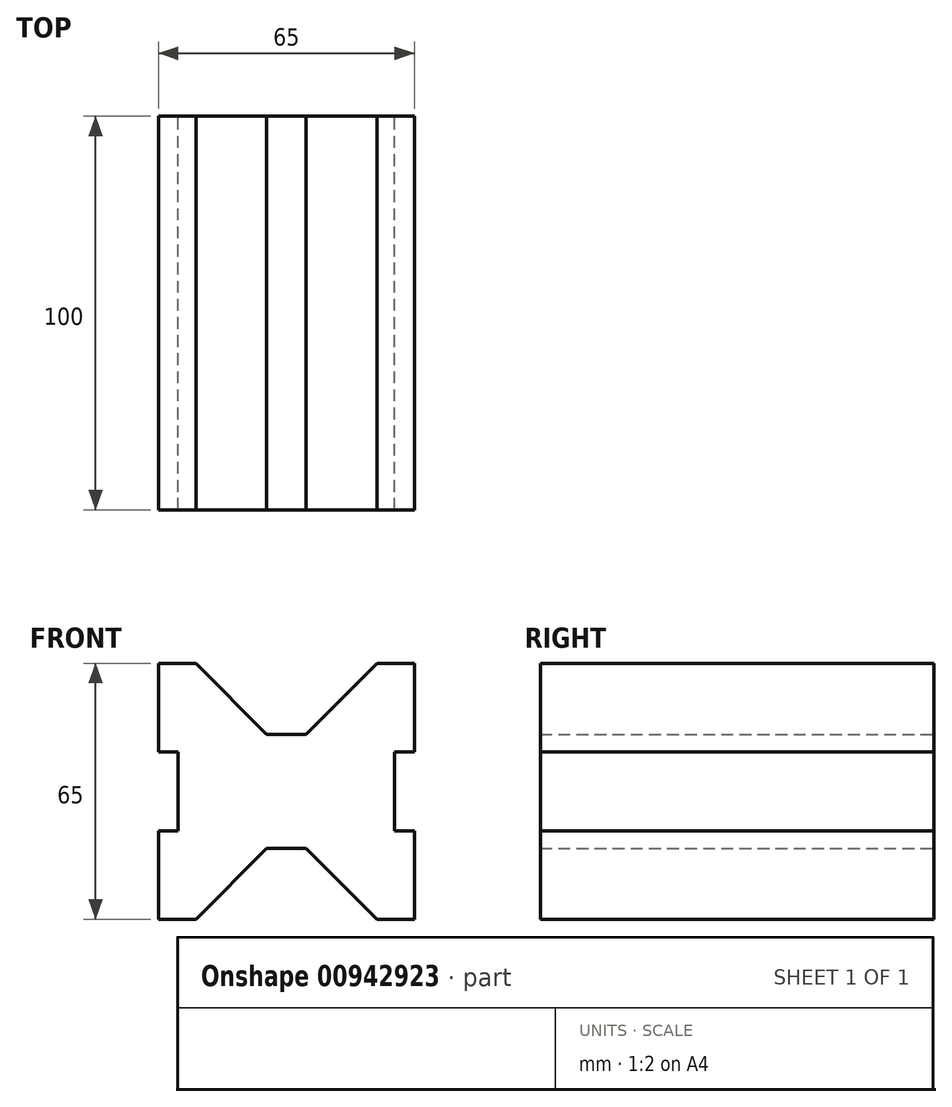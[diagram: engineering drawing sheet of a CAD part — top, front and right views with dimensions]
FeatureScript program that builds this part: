
annotation { "Feature Type Name" : "Feature", "Feature Type Description" : "" }
export const myFeature = defineFeature(function(context is Context, id is Id, definition is map)
    precondition{}
    {
        {
            var Q0;
            Q0=qCreatedBy(makeId("Front.planeOp"),FACE);
            var sketch = newSketch(context, id + "F0", { "sketchPlane" : qUnion([Q0])});
            skLineSegment(sketch, "E0", {"start": v(0, 42.8) * mm, "end": v(0, -43.08) * mm, "construction": true});
            skLineSegment(sketch, "E1", {"start": v(0, 14.5) * mm, "end": v(-5, 14.5) * mm});
            skLineSegment(sketch, "E2", {"start": v(-5, 14.5) * mm, "end": v(-23, 32.5) * mm});
            skLineSegment(sketch, "E3", {"start": v(-23, 32.5) * mm, "end": v(-32.5, 32.5) * mm});
            skLineSegment(sketch, "E4", {"start": v(-32.5, 32.5) * mm, "end": v(-32.5, 10) * mm});
            skLineSegment(sketch, "E5", {"start": v(-32.5, 10) * mm, "end": v(-27.5, 10) * mm});
            skLineSegment(sketch, "E6", {"start": v(-27.5, 10) * mm, "end": v(-27.5, -10) * mm});
            skLineSegment(sketch, "E7", {"start": v(-27.5, -10) * mm, "end": v(-32.5, -10) * mm});
            skLineSegment(sketch, "E8", {"start": v(-32.5, -10) * mm, "end": v(-32.5, -32.5) * mm});
            skLineSegment(sketch, "E9", {"start": v(-32.5, -32.5) * mm, "end": v(-23, -32.5) * mm});
            skLineSegment(sketch, "E10", {"start": v(-5, -14.5) * mm, "end": v(-23, -32.5) * mm});
            skLineSegment(sketch, "E11", {"start": v(-5, -14.5) * mm, "end": v(0, -14.5) * mm});
            skLineSegment(sketch, "E12", {"start": v(0, -14.5) * mm, "end": v(0, 14.5) * mm});
            skLineSegment(sketch, "E13.MirrorCS", {"start": v(0, 14.5) * mm, "end": v(5, 14.5) * mm});
            skLineSegment(sketch, "E14.MirrorCS", {"start": v(5, 14.5) * mm, "end": v(23, 32.5) * mm});
            skLineSegment(sketch, "E15.MirrorCS", {"start": v(23, 32.5) * mm, "end": v(32.5, 32.5) * mm});
            skLineSegment(sketch, "E16.MirrorCS", {"start": v(32.5, 32.5) * mm, "end": v(32.5, 10) * mm});
            skLineSegment(sketch, "E17.MirrorCS", {"start": v(32.5, 10) * mm, "end": v(27.5, 10) * mm});
            skLineSegment(sketch, "E18.MirrorCS", {"start": v(27.5, 10) * mm, "end": v(27.5, -10) * mm});
            skLineSegment(sketch, "E19.MirrorCS", {"start": v(27.5, -10) * mm, "end": v(32.5, -10) * mm});
            skLineSegment(sketch, "E20.MirrorCS", {"start": v(32.5, -10) * mm, "end": v(32.5, -32.5) * mm});
            skLineSegment(sketch, "E21.MirrorCS", {"start": v(32.5, -32.5) * mm, "end": v(23, -32.5) * mm});
            skLineSegment(sketch, "E22.MirrorCS", {"start": v(5, -14.5) * mm, "end": v(23, -32.5) * mm});
            skLineSegment(sketch, "E23.MirrorCS", {"start": v(5, -14.5) * mm, "end": v(0, -14.5) * mm});
            skSolve(sketch);
        }
        {
            var Q0;
            Q0 = qSketchRegion(id + "F0", true);
            extrude(context, id + "F1", {"entities" : qUnion([Q0]), "depth" : 100 * mm, "offsetDistance" : 25 * mm});
        }
    });
